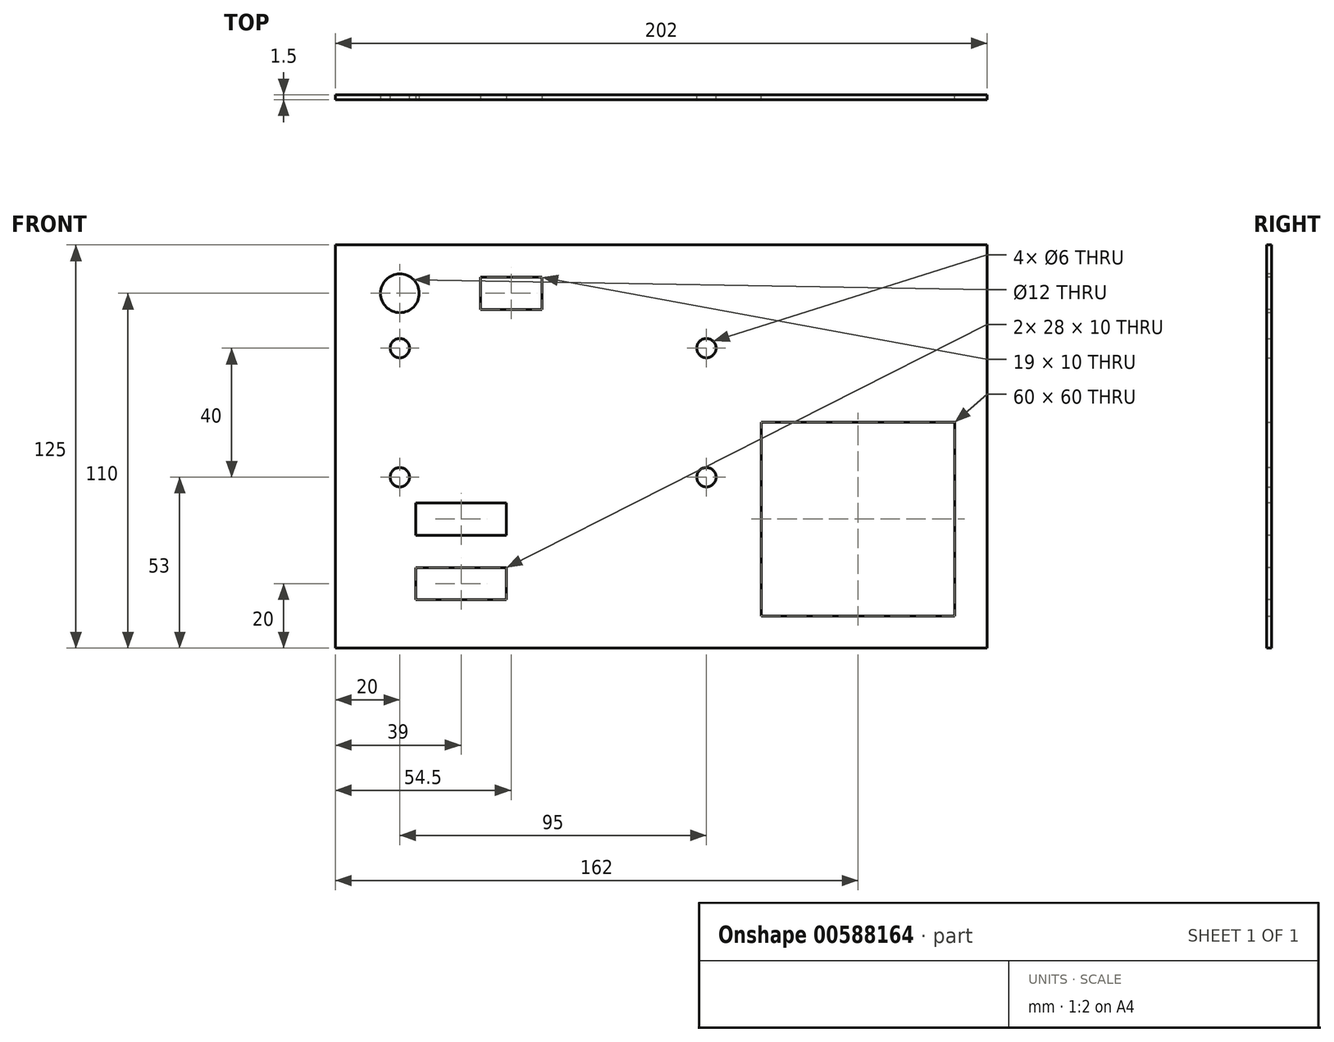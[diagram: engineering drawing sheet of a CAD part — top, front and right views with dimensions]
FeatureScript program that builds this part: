
annotation { "Feature Type Name" : "Feature", "Feature Type Description" : "" }
export const myFeature = defineFeature(function(context is Context, id is Id, definition is map)
    precondition{}
    {
        {
            var Q0;
            Q0=qCreatedBy(makeId("Front.planeOp"),FACE);
            var sketch = newSketch(context, id + "F0", { "sketchPlane" : qUnion([Q0])});
            skLineSegment(sketch, "E0.bottom", {"start": v(0, 0) * mm, "end": v(202, 0) * mm});
            skLineSegment(sketch, "E0.top", {"start": v(0, 125) * mm, "end": v(202, 125) * mm});
            skLineSegment(sketch, "E0.left", {"start": v(0, 0) * mm, "end": v(0, 125) * mm});
            skLineSegment(sketch, "E0.right", {"start": v(202, 0) * mm, "end": v(202, 125) * mm});
            skLineSegment(sketch, "E1.bottom", {"start": v(132, 70) * mm, "end": v(192, 70) * mm});
            skLineSegment(sketch, "E1.top", {"start": v(132, 10) * mm, "end": v(192, 10) * mm});
            skLineSegment(sketch, "E1.left", {"start": v(132, 70) * mm, "end": v(132, 10) * mm});
            skLineSegment(sketch, "E1.right", {"start": v(192, 70) * mm, "end": v(192, 10) * mm});
            skSolve(sketch);
        }
        {
            var Q0;
            Q0 = qSketchRegion(id + "F0", true);
            extrude(context, id + "F1", {"entities" : qUnion([Q0]), "depth" : 1.5 * mm, "offsetDistance" : 25 * mm});
        }
        {
            var Q0;
            Q0=makeQuery(id+"F1.opExtrude","CAP_FACE",FACE,{"disambiguationData":[OSD([sQuery(id+"F0.wireOp",EDGE,"E0.bottom"),sQuery(id+"F0.wireOp",EDGE,"E0.top"),sQuery(id+"F0.wireOp",EDGE,"E0.left"),sQuery(id+"F0.wireOp",EDGE,"E0.right"),sQuery(id+"F0.wireOp",EDGE,"E1.bottom"),sQuery(id+"F0.wireOp",EDGE,"E1.top"),sQuery(id+"F0.wireOp",EDGE,"E1.left"),sQuery(id+"F0.wireOp",EDGE,"E1.right")])],"isStart":false});
            var sketch = newSketch(context, id + "F2", { "sketchPlane" : qUnion([Q0])});
            skLineSegment(sketch, "E2.bottom", {"start": v(25, 25) * mm, "end": v(53, 25) * mm});
            skLineSegment(sketch, "E2.top", {"start": v(25, 15) * mm, "end": v(53, 15) * mm});
            skLineSegment(sketch, "E2.left", {"start": v(25, 25) * mm, "end": v(25, 15) * mm});
            skLineSegment(sketch, "E2.right", {"start": v(53, 25) * mm, "end": v(53, 15) * mm});
            skLineSegment(sketch, "E3", {"start": v(6.6, 30) * mm, "end": v(73.38, 30) * mm, "construction": true});
            skLineSegment(sketch, "E4.MirrorCS", {"start": v(25, 35) * mm, "end": v(53, 35) * mm});
            skLineSegment(sketch, "E5.MirrorCS", {"start": v(25, 45) * mm, "end": v(53, 45) * mm});
            skLineSegment(sketch, "E6.MirrorCS", {"start": v(25, 35) * mm, "end": v(25, 45) * mm});
            skLineSegment(sketch, "E7.MirrorCS", {"start": v(53, 35) * mm, "end": v(53, 45) * mm});
            skCircle(sketch, "E8", {"center": v(20, 110) * mm, "radius": 6 * mm});
            skLineSegment(sketch, "E9.bottom", {"start": v(45, 115) * mm, "end": v(64, 115) * mm});
            skLineSegment(sketch, "E9.top", {"start": v(45, 105) * mm, "end": v(64, 105) * mm});
            skLineSegment(sketch, "E9.left", {"start": v(45, 115) * mm, "end": v(45, 105) * mm});
            skLineSegment(sketch, "E9.right", {"start": v(64, 115) * mm, "end": v(64, 105) * mm});
            skSolve(sketch);
        }
        {
            var Q0;
            Q0 = qSketchRegion(id + "F2", true);
            extrude(context, id + "F3", {"entities" : qUnion([Q0]), "operationType" : NewBodyOperationType.REMOVE, "endBound" : BoundingType.UP_TO_NEXT, "oppositeDirection" : true, "depth" : 25 * mm, "offsetDistance" : 25 * mm});
        }
        {
            var Q0;
            Q0=makeQuery(id+"F1.opExtrude","CAP_FACE",FACE,{"disambiguationData":[OSD([sQuery(id+"F0.wireOp",EDGE,"E0.bottom"),sQuery(id+"F0.wireOp",EDGE,"E0.top"),sQuery(id+"F0.wireOp",EDGE,"E0.left"),sQuery(id+"F0.wireOp",EDGE,"E0.right"),sQuery(id+"F0.wireOp",EDGE,"E1.bottom"),sQuery(id+"F0.wireOp",EDGE,"E1.top"),sQuery(id+"F0.wireOp",EDGE,"E1.left"),sQuery(id+"F0.wireOp",EDGE,"E1.right")])],"isStart":true});
            var sketch = newSketch(context, id + "F4", { "sketchPlane" : qUnion([Q0])});
            skCircle(sketch, "E10.0", {"center": v(-20, 93) * mm, "radius": 3 * mm});
            skCircle(sketch, "E10.1", {"center": v(-115, 53) * mm, "radius": 3 * mm});
            skCircle(sketch, "E10.2", {"center": v(-20, 53) * mm, "radius": 3 * mm});
            skCircle(sketch, "E10.3", {"center": v(-115, 93) * mm, "radius": 3 * mm});
            skSolve(sketch);
        }
        {
            var Q0;
            Q0 = qSketchRegion(id + "F4", true);
            extrude(context, id + "F5", {"entities" : qUnion([Q0]), "operationType" : NewBodyOperationType.REMOVE, "endBound" : BoundingType.UP_TO_NEXT, "oppositeDirection" : true, "depth" : 25 * mm, "offsetDistance" : 25 * mm});
        }
    });
